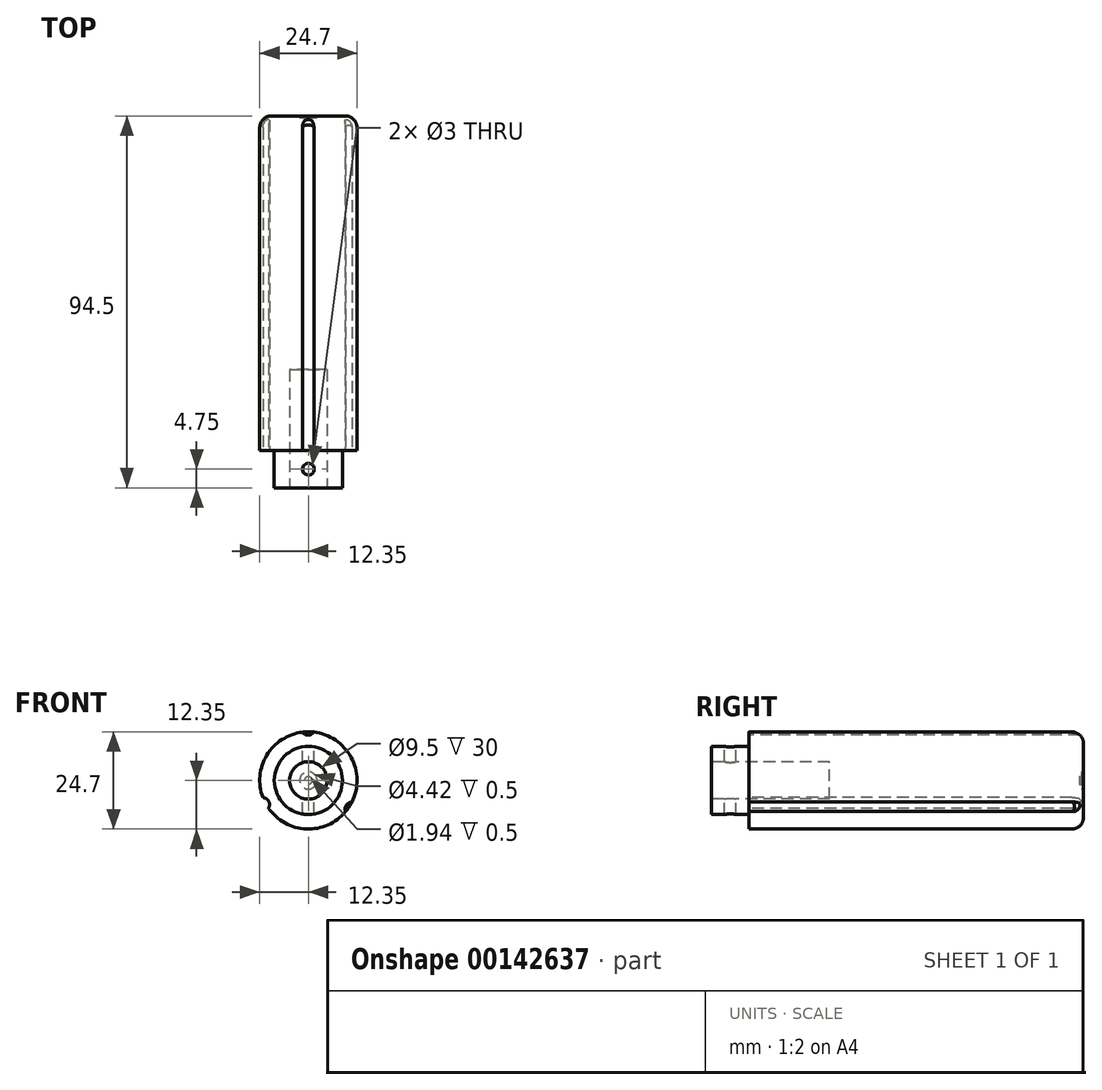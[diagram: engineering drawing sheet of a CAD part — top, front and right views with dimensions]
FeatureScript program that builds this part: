
annotation { "Feature Type Name" : "Feature", "Feature Type Description" : "" }
export const myFeature = defineFeature(function(context is Context, id is Id, definition is map)
    precondition{}
    {
        {
            var Q0;
            Q0=qCreatedBy(makeId("Front.planeOp"),FACE);
            var sketch = newSketch(context, id + "F0", { "sketchPlane" : qUnion([Q0])});
            skCircle(sketch, "E0", {"center": v(0, 0) * mm, "radius": 4.75 * mm});
            skCircle(sketch, "E1", {"center": v(0, 0) * mm, "radius": 8.65 * mm});
            skSolve(sketch);
        }
        {
            var Q0;
            Q0=makeQuery(id+"F0.imprint","IMPRINT",FACE,{"disambiguationData":[TD([[makeQuery(id+"F0.imprint","IMPRINT",EDGE,{"derivedFrom":sQuery(id+"F0.wireOp",EDGE,"E0")}),1.0]])]});
            var Q1;
            Q1=makeQuery(id+"F0.imprint","IMPRINT",FACE,{"disambiguationData":[TD([[makeQuery(id+"F0.imprint","IMPRINT",EDGE,{"derivedFrom":sQuery(id+"F0.wireOp",EDGE,"E0")}),-1.0]])]});
            extrude(context, id + "F1", {"entities" : qUnion([Q0, Q1]), "oppositeDirection" : true, "depth" : 9.5 * mm});
        }
        {
            var Q0;
            Q0=makeQuery(id+"F1.opExtrude","CAP_FACE",FACE,{"disambiguationData":[OSD([sQuery(id+"F0.wireOp",EDGE,"E1")])],"isStart":false});
            var sketch = newSketch(context, id + "F2", { "sketchPlane" : qUnion([Q0])});
            skCircle(sketch, "E2", {"center": v(0, 0) * mm, "radius": 12.35 * mm});
            skSolve(sketch);
        }
        {
            var Q0;
            Q0 = qSketchRegion(id + "F2", true);
            extrude(context, id + "F3", {"entities" : qUnion([Q0]), "operationType" : NewBodyOperationType.ADD, "depth" : 85 * mm});
        }
        {
            var Q0;
            Q0=makeQuery(id+"F1.opExtrude","CAP_FACE",FACE,{"disambiguationData":[OSD([sQuery(id+"F0.wireOp",EDGE,"E1")])],"isStart":true});
            var sketch = newSketch(context, id + "F4", { "sketchPlane" : qUnion([Q0])});
            skCircle(sketch, "E3", {"center": v(0, 0) * mm, "radius": 4.75 * mm});
            skSolve(sketch);
        }
        {
            var Q0;
            Q0=makeQuery(id+"F4.imprint","IMPRINT",FACE,{"disambiguationData":[TD([[makeQuery(id+"F4.imprint","IMPRINT",EDGE,{"derivedFrom":sQuery(id+"F4.wireOp",EDGE,"E3")}),1.0]])]});
            extrude(context, id + "F5", {"entities" : qUnion([Q0]), "operationType" : NewBodyOperationType.REMOVE, "oppositeDirection" : true, "depth" : 30 * mm});
        }
        {
            var Q0;
            Q0=makeQuery(id+"F3.opExtrude","CAP_EDGE",EDGE,{"disambiguationData":[OSD([sQuery(id+"F2.wireOp",EDGE,"E2")])],"isStart":false});
            fillet(context, id + "F6", {"entities" : qUnion([Q0]), "radius" : 3 * mm, "tangentPropagation" : true, "allowEdgeOverflow" : false});
        }
        {
            var Q0;
            Q0=makeQuery(id+"F3.opExtrude","CAP_FACE",FACE,{"disambiguationData":[OSD([sQuery(id+"F2.wireOp",EDGE,"E2")])],"isStart":false});
            var sketch = newSketch(context, id + "F7", { "sketchPlane" : qUnion([Q0])});
            skCircle(sketch, "E4", {"center": v(0, 0) * mm, "radius": 2.2 * mm});
            skSolve(sketch);
        }
        {
            var Q0;
            Q0 = qSketchRegion(id + "F7", true);
            extrude(context, id + "F8", {"entities" : qUnion([Q0]), "operationType" : NewBodyOperationType.REMOVE, "oppositeDirection" : true, "depth" : 0.5 * mm});
        }
        {
            var Q0;
            Q0=makeQuery(id+"F8.boolean.opBoolean","COPY",FACE,{"derivedFrom":makeQuery(id+"F8.opExtrude","CAP_FACE",FACE,{"disambiguationData":[OSD([sQuery(id+"F7.wireOp",EDGE,"E4")])],"isStart":false})});
            var sketch = newSketch(context, id + "F9", { "sketchPlane" : qUnion([Q0])});
            skCircle(sketch, "E5", {"center": v(0, 0) * mm, "radius": 0.97 * mm});
            skSolve(sketch);
        }
        {
            var Q0;
            Q0 = qSketchRegion(id + "F9", true);
            extrude(context, id + "F10", {"entities" : qUnion([Q0]), "operationType" : NewBodyOperationType.REMOVE, "oppositeDirection" : true, "depth" : 0.5 * mm});
        }
        {
            var Q0;
            Q0=makeQuery(id+"F3.opExtrude","CAP_FACE",FACE,{"disambiguationData":[OSD([sQuery(id+"F2.wireOp",EDGE,"E2")])],"isStart":true});
            var sketch = newSketch(context, id + "F11", { "sketchPlane" : qUnion([Q0])});
            skArc(sketch, "E6", {"start": v(-1.5, 12.26) * mm, "mid": v(-0.05, 11.5) * mm, "end": v(1.4, 12.27) * mm});
            skArc(sketch, "E7", {"start": v(11.05, -5.5) * mm, "mid": v(9.62, -6.3) * mm, "end": v(9.47, -7.92) * mm});
            skArc(sketch, "E8", {"start": v(-10.15, -7.04) * mm, "mid": v(-10.08, -5.3) * mm, "end": v(-11.55, -4.36) * mm});
            skLineSegment(sketch, "E9", {"start": v(-1.5, 12.26) * mm, "end": v(1.4, 12.27) * mm});
            skLineSegment(sketch, "E10", {"start": v(11.05, -5.5) * mm, "end": v(9.47, -7.92) * mm});
            skSolve(sketch);
        }
        {
            var Q0;
            Q0 = qSketchRegion(id + "F11", true);
            var Q1;
            {var subQ0=sQuery(id+"F11.wireOp",EDGE,"E8");Q1=makeQuery(id+"F11.imprint","IMPRINT",FACE,{"disambiguationData":[TD([[makeQuery(id+"F11.imprint","IMPRINT",EDGE,{"derivedFrom":subQ0}),1.0]])]});}
            extrude(context, id + "F12", {"entities" : qUnion([Q0, Q1]), "operationType" : NewBodyOperationType.REMOVE, "oppositeDirection" : true, "depth" : 100 * mm});
        }
        {
            var Q0;
            Q0=qCreatedBy(makeId("Top.planeOp"),FACE);
            var sketch = newSketch(context, id + "F13", { "sketchPlane" : qUnion([Q0])});
            skCircle(sketch, "E11", {"center": v(0, 4.75) * mm, "radius": 1.5 * mm});
            skSolve(sketch);
        }
        {
            var Q0;
            Q0=makeQuery(id+"F13.imprint","IMPRINT",FACE,{"disambiguationData":[TD([[makeQuery(id+"F13.imprint","IMPRINT",EDGE,{"derivedFrom":sQuery(id+"F13.wireOp",EDGE,"E11")}),1.0]])]});
            extrude(context, id + "F14", {"entities" : qUnion([Q0]), "operationType" : NewBodyOperationType.REMOVE, "endBound" : BoundingType.SYMMETRIC, "oppositeDirection" : true, "depth" : 100 * mm});
        }
    });
